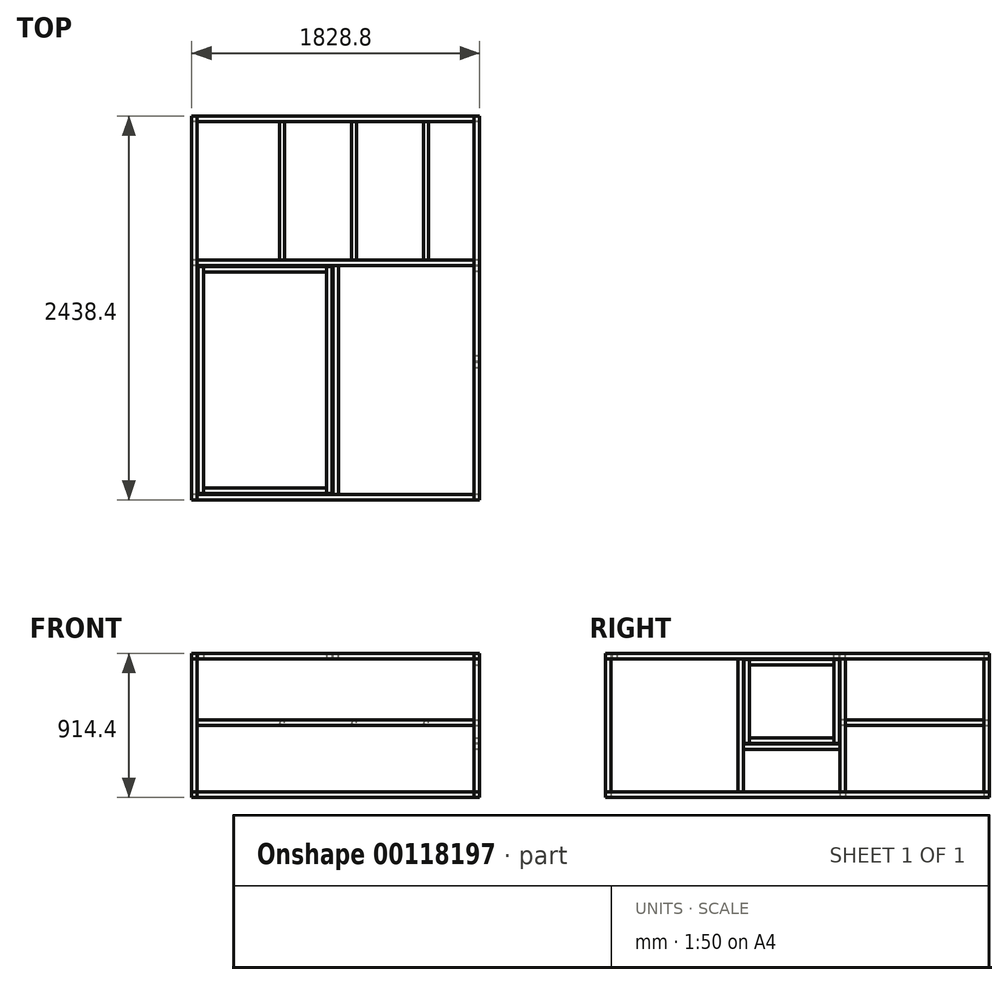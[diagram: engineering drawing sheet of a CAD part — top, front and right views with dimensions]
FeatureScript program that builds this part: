
annotation { "Feature Type Name" : "Feature", "Feature Type Description" : "" }
export const myFeature = defineFeature(function(context is Context, id is Id, definition is map)
    precondition{}
    {
        {
            var Q0;
            Q0=qCreatedBy(makeId("Top.planeOp"),FACE);
            var sketch = newSketch(context, id + "F0", { "sketchPlane" : qUnion([Q0])});
            skLineSegment(sketch, "E0.bottom", {"start": v(-914.4, 1219.2) * mm, "end": v(914.4, 1219.2) * mm});
            skLineSegment(sketch, "E0.top", {"start": v(-914.4, -1219.2) * mm, "end": v(914.4, -1219.2) * mm});
            skLineSegment(sketch, "E0.left", {"start": v(-914.4, 1219.2) * mm, "end": v(-914.4, -1219.2) * mm});
            skLineSegment(sketch, "E0.right", {"start": v(914.4, 1219.2) * mm, "end": v(914.4, -1219.2) * mm});
            skPoint(sketch, "E0.middle", {"position": v(0, 0) * mm});
            skSolve(sketch);
        }
        {
            var Q0;
            Q0=qCreatedBy(makeId("Front.planeOp"),FACE);
            var sketch = newSketch(context, id + "F1", { "sketchPlane" : qUnion([Q0])});
            skLineSegment(sketch, "E1.bottom", {"start": v(-914.4, 0) * mm, "end": v(914.4, 0) * mm});
            skLineSegment(sketch, "E1.top", {"start": v(-914.4, 914.4) * mm, "end": v(914.4, 914.4) * mm});
            skLineSegment(sketch, "E1.left", {"start": v(-914.4, 0) * mm, "end": v(-914.4, 914.4) * mm});
            skLineSegment(sketch, "E1.right", {"start": v(914.4, 0) * mm, "end": v(914.4, 914.4) * mm});
            skSolve(sketch);
        }
        {
            var Q0;
            Q0=qCreatedBy(makeId("Front.planeOp"),FACE);
            var sketch = newSketch(context, id + "F2", { "sketchPlane" : qUnion([Q0])});
            skLineSegment(sketch, "E2.bottom", {"start": v(914.4, 0) * mm, "end": v(879.48, 0) * mm});
            skLineSegment(sketch, "E2.top", {"start": v(914.4, 34.93) * mm, "end": v(879.48, 34.93) * mm});
            skLineSegment(sketch, "E2.left", {"start": v(914.4, 0) * mm, "end": v(914.4, 34.93) * mm});
            skLineSegment(sketch, "E2.right", {"start": v(879.48, 0) * mm, "end": v(879.48, 34.93) * mm});
            skLineSegment(sketch, "E3.bottom", {"start": v(914.4, 914.4) * mm, "end": v(879.47, 914.4) * mm});
            skLineSegment(sketch, "E3.top", {"start": v(914.4, 879.47) * mm, "end": v(879.47, 879.47) * mm});
            skLineSegment(sketch, "E3.left", {"start": v(914.4, 914.4) * mm, "end": v(914.4, 879.47) * mm});
            skLineSegment(sketch, "E3.right", {"start": v(879.47, 914.4) * mm, "end": v(879.47, 879.47) * mm});
            skLineSegment(sketch, "E4.bottom", {"start": v(-914.4, 914.4) * mm, "end": v(-879.48, 914.4) * mm});
            skLineSegment(sketch, "E4.top", {"start": v(-914.4, 879.47) * mm, "end": v(-879.48, 879.47) * mm});
            skLineSegment(sketch, "E4.left", {"start": v(-914.4, 914.4) * mm, "end": v(-914.4, 879.48) * mm});
            skLineSegment(sketch, "E4.right", {"start": v(-879.48, 914.4) * mm, "end": v(-879.48, 879.48) * mm});
            skLineSegment(sketch, "E5.bottom", {"start": v(-914.4, 0) * mm, "end": v(-879.48, 0) * mm});
            skLineSegment(sketch, "E5.top", {"start": v(-914.4, 34.92) * mm, "end": v(-879.48, 34.92) * mm});
            skLineSegment(sketch, "E5.left", {"start": v(-914.4, 0) * mm, "end": v(-914.4, 34.92) * mm});
            skLineSegment(sketch, "E5.right", {"start": v(-879.48, 0) * mm, "end": v(-879.48, 34.92) * mm});
            skSolve(sketch);
        }
        {
            var Q0;
            Q0 = qSketchRegion(id + "F2", true);
            extrude(context, id + "F3", {"entities" : qUnion([Q0]), "endBound" : BoundingType.SYMMETRIC, "depth" : 2438.4 * mm});
        }
        {
            var Q0;
            Q0=makeQuery(id+"F3.opExtrude","SWEPT_FACE",FACE,{"disambiguationData":[OSD([sQuery(id+"F2.wireOp",EDGE,"E5.top")])]});
            var sketch = newSketch(context, id + "F4", { "sketchPlane" : qUnion([Q0])});
            skLineSegment(sketch, "E6.bottom", {"start": v(-879.48, -1219.2) * mm, "end": v(-914.4, -1219.2) * mm});
            skLineSegment(sketch, "E6.top", {"start": v(-879.48, -1184.27) * mm, "end": v(-914.4, -1184.27) * mm});
            skLineSegment(sketch, "E6.left", {"start": v(-879.48, -1219.2) * mm, "end": v(-879.48, -1184.27) * mm});
            skLineSegment(sketch, "E6.right", {"start": v(-914.4, -1219.2) * mm, "end": v(-914.4, -1184.27) * mm});
            skLineSegment(sketch, "E7.bottom", {"start": v(-879.48, 1219.2) * mm, "end": v(-914.4, 1219.2) * mm});
            skLineSegment(sketch, "E7.top", {"start": v(-879.48, 1184.27) * mm, "end": v(-914.4, 1184.27) * mm});
            skLineSegment(sketch, "E7.left", {"start": v(-879.48, 1219.2) * mm, "end": v(-879.48, 1184.27) * mm});
            skLineSegment(sketch, "E7.right", {"start": v(-914.4, 1219.2) * mm, "end": v(-914.4, 1184.28) * mm});
            skLineSegment(sketch, "E8.bottom", {"start": v(914.4, 1219.2) * mm, "end": v(879.48, 1219.2) * mm});
            skLineSegment(sketch, "E8.top", {"start": v(914.4, 1184.27) * mm, "end": v(879.48, 1184.27) * mm});
            skLineSegment(sketch, "E8.left", {"start": v(914.4, 1219.2) * mm, "end": v(914.4, 1184.28) * mm});
            skLineSegment(sketch, "E8.right", {"start": v(879.48, 1219.2) * mm, "end": v(879.48, 1184.27) * mm});
            skLineSegment(sketch, "E9.bottom", {"start": v(914.4, -1219.2) * mm, "end": v(879.48, -1219.2) * mm});
            skLineSegment(sketch, "E9.top", {"start": v(914.4, -1184.27) * mm, "end": v(879.48, -1184.27) * mm});
            skLineSegment(sketch, "E9.left", {"start": v(914.4, -1219.2) * mm, "end": v(914.4, -1184.27) * mm});
            skLineSegment(sketch, "E9.right", {"start": v(879.48, -1219.2) * mm, "end": v(879.48, -1184.27) * mm});
            skLineSegment(sketch, "E10.bottom", {"start": v(-879.48, 269.87) * mm, "end": v(-914.4, 269.87) * mm});
            skLineSegment(sketch, "E10.top", {"start": v(-879.48, 304.8) * mm, "end": v(-914.4, 304.8) * mm});
            skLineSegment(sketch, "E10.left", {"start": v(-879.48, 269.87) * mm, "end": v(-879.48, 304.8) * mm});
            skLineSegment(sketch, "E10.right", {"start": v(-914.4, 269.87) * mm, "end": v(-914.4, 304.8) * mm});
            skLineSegment(sketch, "E11.bottom", {"start": v(914.4, 269.87) * mm, "end": v(879.48, 269.87) * mm});
            skLineSegment(sketch, "E11.top", {"start": v(914.4, 304.8) * mm, "end": v(879.48, 304.8) * mm});
            skLineSegment(sketch, "E11.left", {"start": v(914.4, 269.87) * mm, "end": v(914.4, 304.8) * mm});
            skLineSegment(sketch, "E11.right", {"start": v(879.48, 269.87) * mm, "end": v(879.48, 304.8) * mm});
            skLineSegment(sketch, "E12", {"start": v(-879.48, 287.34) * mm, "end": v(879.48, 287.34) * mm, "construction": true});
            skSolve(sketch);
        }
        {
            var Q0;
            Q0 = qSketchRegion(id + "F4", true);
            var Q1;
            Q1=makeQuery(id+"F3.opExtrude","SWEPT_FACE",FACE,{"disambiguationData":[OSD([sQuery(id+"F2.wireOp",EDGE,"E4.top")])]});
            extrude(context, id + "F5", {"entities" : qUnion([Q0]), "endBound" : BoundingType.UP_TO_SURFACE, "endBoundEntityFace" : qUnion([Q1]), "depth" : 25.4 * mm});
        }
        {
            var Q0;
            Q0=makeQuery(id+"F3.opExtrude","SWEPT_FACE",FACE,{"disambiguationData":[OSD([sQuery(id+"F2.wireOp",EDGE,"E4.right")])]});
            var sketch = newSketch(context, id + "F6", { "sketchPlane" : qUnion([Q0])});
            skLineSegment(sketch, "E13.bottom", {"start": v(269.87, 879.48) * mm, "end": v(304.8, 879.48) * mm});
            skLineSegment(sketch, "E13.top", {"start": v(269.87, 914.4) * mm, "end": v(304.8, 914.4) * mm});
            skLineSegment(sketch, "E13.left", {"start": v(269.87, 879.48) * mm, "end": v(269.87, 914.4) * mm});
            skLineSegment(sketch, "E13.right", {"start": v(304.8, 879.48) * mm, "end": v(304.8, 914.4) * mm});
            skLineSegment(sketch, "E14.bottom", {"start": v(-1219.2, 914.4) * mm, "end": v(-1184.27, 914.4) * mm});
            skLineSegment(sketch, "E14.top", {"start": v(-1219.2, 879.48) * mm, "end": v(-1184.27, 879.48) * mm});
            skLineSegment(sketch, "E14.left", {"start": v(-1219.2, 914.4) * mm, "end": v(-1219.2, 879.48) * mm});
            skLineSegment(sketch, "E14.right", {"start": v(-1184.27, 914.4) * mm, "end": v(-1184.27, 879.48) * mm});
            skLineSegment(sketch, "E15.bottom", {"start": v(1219.2, 914.4) * mm, "end": v(1184.27, 914.4) * mm});
            skLineSegment(sketch, "E15.top", {"start": v(1219.2, 879.48) * mm, "end": v(1184.27, 879.48) * mm});
            skLineSegment(sketch, "E15.left", {"start": v(1219.2, 914.4) * mm, "end": v(1219.2, 879.48) * mm});
            skLineSegment(sketch, "E15.right", {"start": v(1184.27, 914.4) * mm, "end": v(1184.27, 879.48) * mm});
            skLineSegment(sketch, "E16.bottom", {"start": v(1219.2, 0) * mm, "end": v(1184.27, 0) * mm});
            skLineSegment(sketch, "E16.top", {"start": v(1219.2, 34.92) * mm, "end": v(1184.27, 34.92) * mm});
            skLineSegment(sketch, "E16.left", {"start": v(1219.2, 34.92) * mm, "end": v(1219.2, 0) * mm});
            skLineSegment(sketch, "E16.right", {"start": v(1184.27, 34.92) * mm, "end": v(1184.27, 0) * mm});
            skLineSegment(sketch, "E17.bottom", {"start": v(-1184.27, 34.92) * mm, "end": v(-1219.2, 34.92) * mm});
            skLineSegment(sketch, "E17.top", {"start": v(-1184.27, 0) * mm, "end": v(-1219.2, 0) * mm});
            skLineSegment(sketch, "E17.left", {"start": v(-1184.27, 34.92) * mm, "end": v(-1184.27, 0) * mm});
            skLineSegment(sketch, "E17.right", {"start": v(-1219.2, 34.92) * mm, "end": v(-1219.2, 0) * mm});
            skLineSegment(sketch, "E18.bottom", {"start": v(269.87, 34.92) * mm, "end": v(304.8, 34.92) * mm});
            skLineSegment(sketch, "E18.top", {"start": v(269.87, 0) * mm, "end": v(304.8, 0) * mm});
            skLineSegment(sketch, "E18.left", {"start": v(269.87, 34.92) * mm, "end": v(269.87, 0) * mm});
            skLineSegment(sketch, "E18.right", {"start": v(304.8, 34.92) * mm, "end": v(304.8, 0) * mm});
            skLineSegment(sketch, "E19.bottom", {"start": v(304.8, 457.2) * mm, "end": v(269.87, 457.2) * mm});
            skLineSegment(sketch, "E19.top", {"start": v(304.8, 492.12) * mm, "end": v(269.87, 492.12) * mm});
            skLineSegment(sketch, "E19.left", {"start": v(304.8, 457.2) * mm, "end": v(304.8, 492.12) * mm});
            skLineSegment(sketch, "E19.right", {"start": v(269.87, 457.2) * mm, "end": v(269.87, 492.12) * mm});
            skLineSegment(sketch, "E20.bottom", {"start": v(1184.27, 492.12) * mm, "end": v(1219.2, 492.12) * mm});
            skLineSegment(sketch, "E20.top", {"start": v(1184.27, 457.2) * mm, "end": v(1219.2, 457.2) * mm});
            skLineSegment(sketch, "E20.left", {"start": v(1184.27, 492.12) * mm, "end": v(1184.27, 457.2) * mm});
            skLineSegment(sketch, "E20.right", {"start": v(1219.2, 492.12) * mm, "end": v(1219.2, 457.2) * mm});
            skSolve(sketch);
        }
        {
            var Q0;
            Q0 = qSketchRegion(id + "F6", true);
            var Q1;
            Q1=makeQuery(id+"F3.opExtrude","SWEPT_FACE",FACE,{"disambiguationData":[OSD([sQuery(id+"F2.wireOp",EDGE,"E3.right")])]});
            extrude(context, id + "F7", {"entities" : qUnion([Q0]), "endBound" : BoundingType.UP_TO_SURFACE, "endBoundEntityFace" : qUnion([Q1]), "depth" : 25.4 * mm});
        }
        {
            var Q0;
            Q0=makeQuery(id+"F7.opExtrude","SWEPT_FACE",FACE,{"disambiguationData":[OSD([sQuery(id+"F6.wireOp",EDGE,"E20.left")])]});
            var sketch = newSketch(context, id + "F8", { "sketchPlane" : qUnion([Q0])});
            skCircle(sketch, "E21", {"center": v(574.68, 474.66) * mm, "radius": 15.88 * mm});
            skCircle(sketch, "E22", {"center": v(117.47, 474.66) * mm, "radius": 15.88 * mm});
            skCircle(sketch, "E23", {"center": v(-339.73, 474.66) * mm, "radius": 15.88 * mm});
            skLineSegment(sketch, "E24", {"start": v(574.68, 474.66) * mm, "end": v(-339.73, 474.66) * mm, "construction": true});
            skSolve(sketch);
        }
        {
            var Q0;
            Q0 = qSketchRegion(id + "F8", true);
            var Q1;
            Q1=makeQuery(id+"F7.opExtrude","SWEPT_FACE",FACE,{"disambiguationData":[OSD([sQuery(id+"F6.wireOp",EDGE,"E19.left")])]});
            extrude(context, id + "F9", {"entities" : qUnion([Q0]), "endBound" : BoundingType.UP_TO_SURFACE, "endBoundEntityFace" : qUnion([Q1]), "depth" : 25.4 * mm});
        }
        {
            var Q0;
            Q0=makeQuery(id+"F5.opExtrude","SWEPT_FACE",FACE,{"disambiguationData":[OSD([sQuery(id+"F4.wireOp",EDGE,"E8.top")])]});
            var sketch = newSketch(context, id + "F10", { "sketchPlane" : qUnion([Q0])});
            skLineSegment(sketch, "E25.bottom", {"start": v(879.48, 492.12) * mm, "end": v(914.4, 492.12) * mm});
            skLineSegment(sketch, "E25.top", {"start": v(879.48, 457.2) * mm, "end": v(914.4, 457.2) * mm});
            skLineSegment(sketch, "E25.left", {"start": v(879.48, 492.13) * mm, "end": v(879.48, 457.2) * mm});
            skLineSegment(sketch, "E25.right", {"start": v(914.4, 492.12) * mm, "end": v(914.4, 457.2) * mm});
            skSolve(sketch);
        }
        {
            var Q0;
            Q0 = qSketchRegion(id + "F10", true);
            var Q1;
            Q1=makeQuery(id+"F5.opExtrude","SWEPT_FACE",FACE,{"disambiguationData":[OSD([sQuery(id+"F4.wireOp",EDGE,"E11.top")])]});
            extrude(context, id + "F11", {"entities" : qUnion([Q0]), "endBound" : BoundingType.UP_TO_SURFACE, "endBoundEntityFace" : qUnion([Q1]), "depth" : 25.4 * mm});
        }
        {
            var Q0;
            Q0=makeQuery(id+"F7.opExtrude","SWEPT_FACE",FACE,{"disambiguationData":[OSD([sQuery(id+"F6.wireOp",EDGE,"E14.right")])]});
            var sketch = newSketch(context, id + "F12", { "sketchPlane" : qUnion([Q0])});
            skLineSegment(sketch, "E26.bottom", {"start": v(-17.46, 914.4) * mm, "end": v(17.46, 914.4) * mm});
            skLineSegment(sketch, "E26.top", {"start": v(-17.46, 879.48) * mm, "end": v(17.46, 879.48) * mm});
            skLineSegment(sketch, "E26.left", {"start": v(-17.46, 914.4) * mm, "end": v(-17.46, 879.48) * mm});
            skLineSegment(sketch, "E26.right", {"start": v(17.46, 914.4) * mm, "end": v(17.46, 879.48) * mm});
            skLineSegment(sketch, "E27", {"start": v(0, 879.48) * mm, "end": v(0, 837.85) * mm, "construction": true});
            skSolve(sketch);
        }
        {
            var Q0;
            Q0 = qSketchRegion(id + "F12", true);
            var Q1;
            Q1=makeQuery(id+"F7.opExtrude","SWEPT_FACE",FACE,{"disambiguationData":[OSD([sQuery(id+"F6.wireOp",EDGE,"E13.left")])]});
            extrude(context, id + "F13", {"entities" : qUnion([Q0]), "endBound" : BoundingType.UP_TO_SURFACE, "endBoundEntityFace" : qUnion([Q1]), "depth" : 25.4 * mm});
        }
        {
            var Q0;
            Q0=makeQuery(id+"F13.opExtrude","SWEPT_FACE",FACE,{"disambiguationData":[OSD([sQuery(id+"F12.wireOp",EDGE,"E26.bottom")])]});
            var sketch = newSketch(context, id + "F14", { "sketchPlane" : qUnion([Q0])});
            skLineSegment(sketch, "E28.bottom", {"start": v(-873.13, 263.52) * mm, "end": v(-23.81, 263.52) * mm});
            skLineSegment(sketch, "E28.top", {"start": v(-873.13, -1177.92) * mm, "end": v(-23.81, -1177.92) * mm});
            skLineSegment(sketch, "E28.left", {"start": v(-873.13, 263.52) * mm, "end": v(-873.13, -1177.92) * mm});
            skLineSegment(sketch, "E28.right", {"start": v(-23.81, 263.52) * mm, "end": v(-23.81, -1177.92) * mm});
            skSolve(sketch);
        }
        {
            var Q0;
            Q0=sQuery(id+"F14.wireOp",EDGE,"E28.right");
            var Q1;
            Q1=sQuery(id+"F14.wireOp",VERTEX,"E28.right.start");
            cPlane(context, id + "F15", {"entities" : qUnion([Q0, Q1]), "cplaneType" : CPlaneType.LINE_POINT, "offset" : 25.4 * mm, "width" : 152.4 * mm, "height" : 152.4 * mm});
        }
        {
            var Q0;
            Q0=qCreatedBy(id+"F15.planeOp",FACE);
            var sketch = newSketch(context, id + "F16", { "sketchPlane" : qUnion([Q0])});
            skLineSegment(sketch, "E29.bottom", {"start": v(-23.81, 914.4) * mm, "end": v(-58.74, 914.4) * mm});
            skLineSegment(sketch, "E29.top", {"start": v(-23.81, 879.47) * mm, "end": v(-58.74, 879.47) * mm});
            skLineSegment(sketch, "E29.left", {"start": v(-23.81, 914.4) * mm, "end": v(-23.81, 879.47) * mm});
            skLineSegment(sketch, "E29.right", {"start": v(-58.74, 914.4) * mm, "end": v(-58.74, 879.47) * mm});
            skLineSegment(sketch, "E30.bottom", {"start": v(-873.13, 914.4) * mm, "end": v(-838.2, 914.4) * mm});
            skLineSegment(sketch, "E30.top", {"start": v(-873.13, 879.48) * mm, "end": v(-838.2, 879.48) * mm});
            skLineSegment(sketch, "E30.left", {"start": v(-873.13, 914.4) * mm, "end": v(-873.13, 879.48) * mm});
            skLineSegment(sketch, "E30.right", {"start": v(-838.2, 914.4) * mm, "end": v(-838.2, 879.48) * mm});
            skSolve(sketch);
        }
        {
            var Q0;
            Q0 = qSketchRegion(id + "F16", true);
            extrude(context, id + "F17", {"entities" : qUnion([Q0]), "depth" : 1441.45 * mm});
        }
        {
            var Q0;
            Q0=makeQuery(id+"F17.opExtrude","SWEPT_FACE",FACE,{"disambiguationData":[OSD([sQuery(id+"F16.wireOp",EDGE,"E29.right")])]});
            var sketch = newSketch(context, id + "F18", { "sketchPlane" : qUnion([Q0])});
            skLineSegment(sketch, "E31.bottom", {"start": v(-263.52, 879.47) * mm, "end": v(-228.6, 879.47) * mm});
            skLineSegment(sketch, "E31.top", {"start": v(-263.52, 914.4) * mm, "end": v(-228.6, 914.4) * mm});
            skLineSegment(sketch, "E31.left", {"start": v(-263.52, 879.47) * mm, "end": v(-263.52, 914.4) * mm});
            skLineSegment(sketch, "E31.right", {"start": v(-228.6, 879.47) * mm, "end": v(-228.6, 914.4) * mm});
            skLineSegment(sketch, "E32.bottom", {"start": v(1177.93, 914.4) * mm, "end": v(1143, 914.4) * mm});
            skLineSegment(sketch, "E32.top", {"start": v(1177.93, 879.47) * mm, "end": v(1143, 879.47) * mm});
            skLineSegment(sketch, "E32.left", {"start": v(1177.93, 914.4) * mm, "end": v(1177.93, 879.47) * mm});
            skLineSegment(sketch, "E32.right", {"start": v(1143, 914.4) * mm, "end": v(1143, 879.47) * mm});
            skSolve(sketch);
        }
        {
            var Q0;
            Q0 = qSketchRegion(id + "F18", true);
            var Q1;
            Q1=makeQuery(id+"F17.opExtrude","SWEPT_FACE",FACE,{"disambiguationData":[OSD([sQuery(id+"F16.wireOp",EDGE,"E30.right")])]});
            extrude(context, id + "F19", {"entities" : qUnion([Q0]), "endBound" : BoundingType.UP_TO_SURFACE, "endBoundEntityFace" : qUnion([Q1]), "depth" : 25.4 * mm});
        }
        {
            var Q0;
            Q0=makeQuery(id+"F3.opExtrude","SWEPT_FACE",FACE,{"disambiguationData":[OSD([sQuery(id+"F2.wireOp",EDGE,"E2.top")])]});
            var sketch = newSketch(context, id + "F20", { "sketchPlane" : qUnion([Q0])});
            skLineSegment(sketch, "E33.bottom", {"start": v(914.4, -377.83) * mm, "end": v(879.48, -377.83) * mm});
            skLineSegment(sketch, "E33.top", {"start": v(914.4, -342.9) * mm, "end": v(879.48, -342.9) * mm});
            skLineSegment(sketch, "E33.left", {"start": v(914.4, -377.83) * mm, "end": v(914.4, -342.9) * mm});
            skLineSegment(sketch, "E33.right", {"start": v(879.48, -377.83) * mm, "end": v(879.48, -342.9) * mm});
            skSolve(sketch);
        }
        {
            var Q0;
            Q0 = qSketchRegion(id + "F20", true);
            var Q1;
            Q1=makeQuery(id+"F3.opExtrude","SWEPT_FACE",FACE,{"disambiguationData":[OSD([sQuery(id+"F2.wireOp",EDGE,"E3.top")])]});
            extrude(context, id + "F21", {"entities" : qUnion([Q0]), "endBound" : BoundingType.UP_TO_SURFACE, "endBoundEntityFace" : qUnion([Q1]), "depth" : 25.4 * mm});
        }
        {
            var Q0;
            Q0=makeQuery(id+"F5.opExtrude","SWEPT_FACE",FACE,{"disambiguationData":[OSD([sQuery(id+"F4.wireOp",EDGE,"E11.bottom")])]});
            var sketch = newSketch(context, id + "F22", { "sketchPlane" : qUnion([Q0])});
            skLineSegment(sketch, "E34.bottom", {"start": v(914.4, 304.8) * mm, "end": v(879.48, 304.8) * mm});
            skLineSegment(sketch, "E34.top", {"start": v(914.4, 339.72) * mm, "end": v(879.48, 339.72) * mm});
            skLineSegment(sketch, "E34.left", {"start": v(914.4, 304.8) * mm, "end": v(914.4, 339.72) * mm});
            skLineSegment(sketch, "E34.right", {"start": v(879.48, 304.8) * mm, "end": v(879.48, 339.72) * mm});
            skSolve(sketch);
        }
        {
            var Q0;
            Q0 = qSketchRegion(id + "F22", true);
            var Q1;
            Q1=makeQuery(id+"F21.opExtrude","SWEPT_FACE",FACE,{"disambiguationData":[OSD([sQuery(id+"F20.wireOp",EDGE,"E33.top")])]});
            extrude(context, id + "F23", {"entities" : qUnion([Q0]), "endBound" : BoundingType.UP_TO_SURFACE, "endBoundEntityFace" : qUnion([Q1]), "depth" : 25.4 * mm});
        }
        {
            var Q0;
            Q0=makeQuery(id+"F3.opExtrude","SWEPT_FACE",FACE,{"disambiguationData":[OSD([sQuery(id+"F2.wireOp",EDGE,"E3.left")])]});
            var sketch = newSketch(context, id + "F24", { "sketchPlane" : qUnion([Q0])});
            skLineSegment(sketch, "E35.bottom", {"start": v(-339.73, 876.3) * mm, "end": v(266.7, 876.3) * mm});
            skLineSegment(sketch, "E35.top", {"start": v(-339.73, 342.9) * mm, "end": v(266.7, 342.9) * mm});
            skLineSegment(sketch, "E35.left", {"start": v(-339.73, 876.3) * mm, "end": v(-339.73, 342.9) * mm});
            skLineSegment(sketch, "E35.right", {"start": v(266.7, 876.3) * mm, "end": v(266.7, 342.9) * mm});
            skSolve(sketch);
        }
        {
            var Q0;
            Q0=sQuery(id+"F24.wireOp",EDGE,"E35.left");
            var Q1;
            Q1=sQuery(id+"F24.wireOp",VERTEX,"E35.bottom.start");
            cPlane(context, id + "F25", {"entities" : qUnion([Q0, Q1]), "cplaneType" : CPlaneType.LINE_POINT, "offset" : 25.4 * mm, "width" : 152.4 * mm, "height" : 152.4 * mm});
        }
        {
            var Q0;
            Q0=qCreatedBy(id+"F25.planeOp",FACE);
            var sketch = newSketch(context, id + "F26", { "sketchPlane" : qUnion([Q0])});
            skLineSegment(sketch, "E36.bottom", {"start": v(914.4, 339.73) * mm, "end": v(879.48, 339.73) * mm});
            skLineSegment(sketch, "E36.top", {"start": v(914.4, 304.8) * mm, "end": v(879.48, 304.8) * mm});
            skLineSegment(sketch, "E36.left", {"start": v(914.4, 339.73) * mm, "end": v(914.4, 304.8) * mm});
            skLineSegment(sketch, "E36.right", {"start": v(879.48, 339.73) * mm, "end": v(879.48, 304.8) * mm});
            skLineSegment(sketch, "E37.bottom", {"start": v(914.4, -266.7) * mm, "end": v(879.48, -266.7) * mm});
            skLineSegment(sketch, "E37.top", {"start": v(914.4, -231.77) * mm, "end": v(879.48, -231.77) * mm});
            skLineSegment(sketch, "E37.left", {"start": v(914.4, -266.7) * mm, "end": v(914.4, -231.77) * mm});
            skLineSegment(sketch, "E37.right", {"start": v(879.48, -266.7) * mm, "end": v(879.48, -231.77) * mm});
            skSolve(sketch);
        }
        {
            var Q0;
            Q0 = qSketchRegion(id + "F26", true);
            extrude(context, id + "F27", {"entities" : qUnion([Q0]), "depth" : 533.4 * mm});
        }
        {
            var Q0;
            Q0=makeQuery(id+"F27.opExtrude","SWEPT_FACE",FACE,{"disambiguationData":[OSD([sQuery(id+"F26.wireOp",EDGE,"E37.top")])]});
            var sketch = newSketch(context, id + "F28", { "sketchPlane" : qUnion([Q0])});
            skLineSegment(sketch, "E38.bottom", {"start": v(914.4, 876.3) * mm, "end": v(879.47, 876.3) * mm});
            skLineSegment(sketch, "E38.top", {"start": v(914.4, 841.38) * mm, "end": v(879.47, 841.38) * mm});
            skLineSegment(sketch, "E38.left", {"start": v(914.4, 876.3) * mm, "end": v(914.4, 841.38) * mm});
            skLineSegment(sketch, "E38.right", {"start": v(879.47, 876.3) * mm, "end": v(879.47, 841.38) * mm});
            skLineSegment(sketch, "E39.bottom", {"start": v(914.4, 342.9) * mm, "end": v(879.48, 342.9) * mm});
            skLineSegment(sketch, "E39.top", {"start": v(914.4, 377.82) * mm, "end": v(879.48, 377.82) * mm});
            skLineSegment(sketch, "E39.left", {"start": v(914.4, 342.9) * mm, "end": v(914.4, 377.82) * mm});
            skLineSegment(sketch, "E39.right", {"start": v(879.48, 342.9) * mm, "end": v(879.48, 377.82) * mm});
            skSolve(sketch);
        }
        {
            var Q0;
            Q0 = qSketchRegion(id + "F28", true);
            var Q1;
            Q1=makeQuery(id+"F27.opExtrude","SWEPT_FACE",FACE,{"disambiguationData":[OSD([sQuery(id+"F26.wireOp",EDGE,"E36.top")])]});
            extrude(context, id + "F29", {"entities" : qUnion([Q0]), "endBound" : BoundingType.UP_TO_SURFACE, "endBoundEntityFace" : qUnion([Q1]), "depth" : 25.4 * mm});
        }
    });
